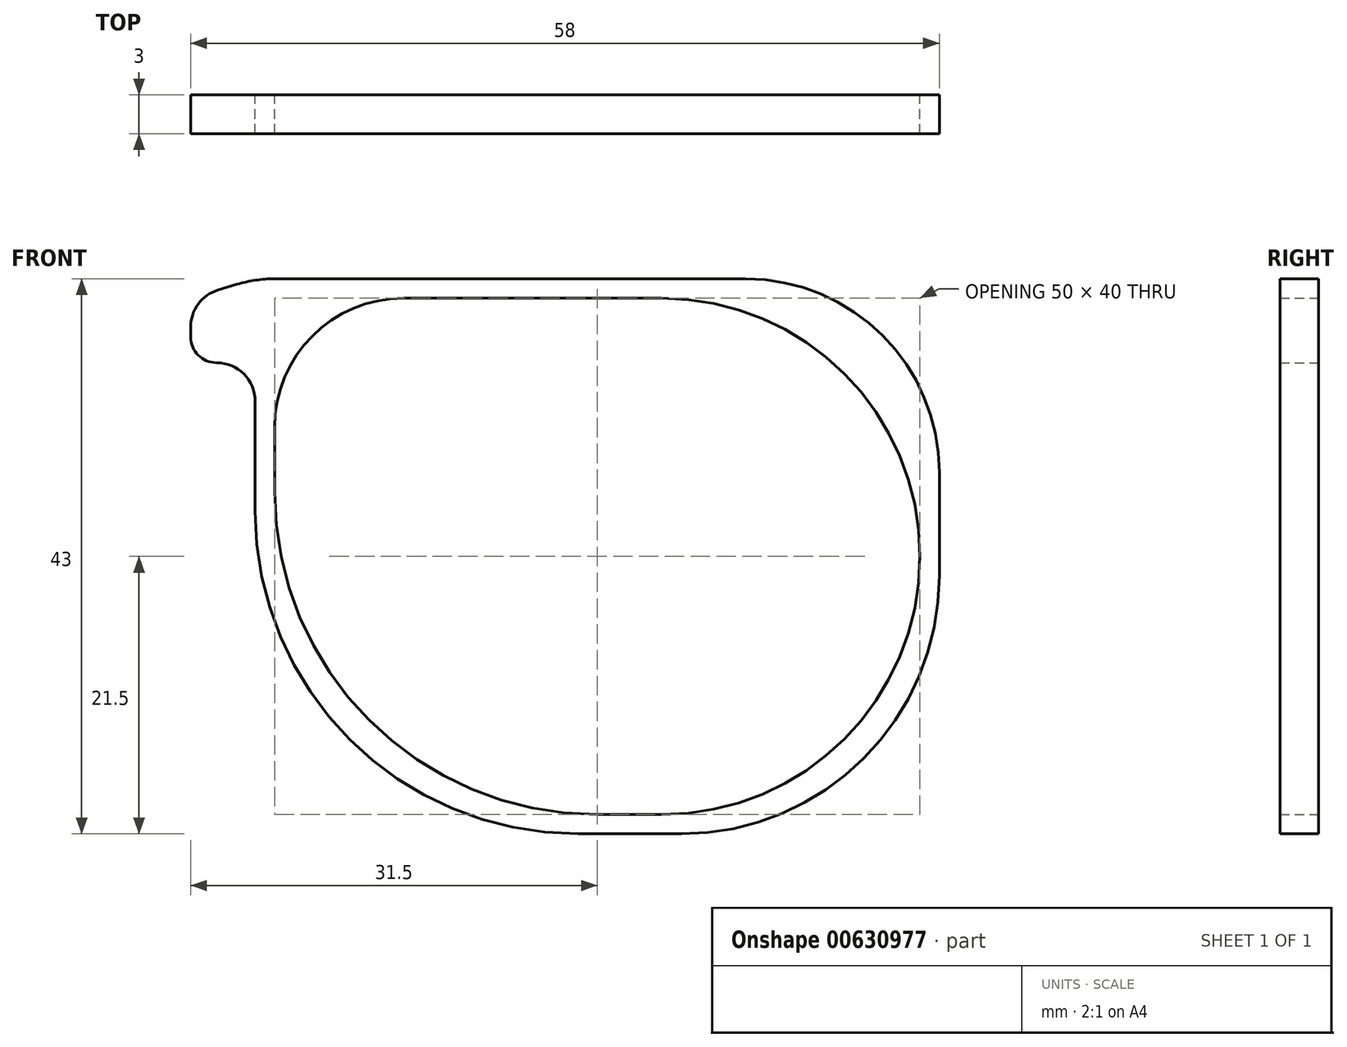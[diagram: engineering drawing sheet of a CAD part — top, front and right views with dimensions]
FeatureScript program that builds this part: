
annotation { "Feature Type Name" : "Feature", "Feature Type Description" : "" }
export const myFeature = defineFeature(function(context is Context, id is Id, definition is map)
    precondition{}
    {
        {
            var Q0;
            Q0=qCreatedBy(makeId("Front.planeOp"),FACE);
            var sketch = newSketch(context, id + "F0", { "sketchPlane" : qUnion([Q0])});
            skLineSegment(sketch, "E0.bottom", {"start": v(5, 20) * mm, "end": v(-15, 20) * mm});
            skLineSegment(sketch, "E0.top", {"start": v(5, -20) * mm, "end": v(0, -20) * mm});
            skLineSegment(sketch, "E0.left", {"start": v(25, 0) * mm, "end": v(25, 0) * mm});
            skLineSegment(sketch, "E0.right", {"start": v(-25, 10) * mm, "end": v(-25, 5) * mm});
            skPoint(sketch, "E0.middle", {"position": v(0, 0) * mm});
            skPoint(sketch, "E1.visualSharp", {"position": v(-25, -20) * mm});
            skArc(sketch, "E1.filletArc", {"start": v(-25, 5) * mm, "mid": v(-17.68, -12.68) * mm, "end": v(0, -20) * mm});
            skPoint(sketch, "E2.visualSharp", {"position": v(25, -20) * mm});
            skArc(sketch, "E2.filletArc", {"start": v(5, -20) * mm, "mid": v(19.14, -14.14) * mm, "end": v(25, 0) * mm});
            skPoint(sketch, "E3.visualSharp", {"position": v(-25, 20) * mm});
            skArc(sketch, "E3.filletArc", {"start": v(-15, 20) * mm, "mid": v(-22.07, 17.07) * mm, "end": v(-25, 10) * mm});
            skPoint(sketch, "E4.visualSharp", {"position": v(25, 20) * mm});
            skArc(sketch, "E4.filletArc", {"start": v(25, 0) * mm, "mid": v(19.14, 14.14) * mm, "end": v(5, 20) * mm});
            skLineSegment(sketch, "E5.bottom", {"start": v(11.5, 21.5) * mm, "end": v(-25.03, 21.5) * mm});
            skLineSegment(sketch, "E5.top", {"start": v(6.5, -21.5) * mm, "end": v(-1.5, -21.5) * mm});
            skLineSegment(sketch, "E5.left", {"start": v(26.5, 6.5) * mm, "end": v(26.5, -1.5) * mm});
            skLineSegment(sketch, "E5.right", {"start": v(-26.5, 12) * mm, "end": v(-26.5, 3.5) * mm});
            skPoint(sketch, "E6.visualSharp", {"position": v(-26.5, -21.5) * mm});
            skArc(sketch, "E6.filletArc", {"start": v(-26.5, 3.5) * mm, "mid": v(-19.18, -14.18) * mm, "end": v(-1.5, -21.5) * mm});
            skPoint(sketch, "E7.visualSharp", {"position": v(26.5, -21.5) * mm});
            skArc(sketch, "E7.filletArc", {"start": v(6.5, -21.5) * mm, "mid": v(20.64, -15.64) * mm, "end": v(26.5, -1.5) * mm});
            skLineSegment(sketch, "E8", {"start": v(-29.5, 15) * mm, "end": v(-29.5, 15) * mm});
            skLineSegment(sketch, "E9", {"start": v(-31.5, 17) * mm, "end": v(-31.5, 17.77) * mm});
            skLineSegment(sketch, "E10", {"start": v(-29.36, 20.64) * mm, "end": v(-27.9, 21.08) * mm});
            skPoint(sketch, "E11.visualSharp", {"position": v(-26.5, 15) * mm});
            skArc(sketch, "E11.filletArc", {"start": v(-26.5, 12) * mm, "mid": v(-27.38, 14.12) * mm, "end": v(-29.5, 15) * mm});
            skPoint(sketch, "E12.visualSharp", {"position": v(-26.5, 21.5) * mm});
            skArc(sketch, "E12.filletArc", {"start": v(-25.03, 21.5) * mm, "mid": v(-26.48, 21.4) * mm, "end": v(-27.9, 21.08) * mm});
            skPoint(sketch, "E13.visualSharp", {"position": v(-31.5, 20) * mm});
            skArc(sketch, "E13.filletArc", {"start": v(-29.36, 20.64) * mm, "mid": v(-30.9, 19.56) * mm, "end": v(-31.5, 17.77) * mm});
            skPoint(sketch, "E14.visualSharp", {"position": v(-31.5, 15) * mm});
            skArc(sketch, "E14.filletArc", {"start": v(-31.5, 17) * mm, "mid": v(-30.91, 15.59) * mm, "end": v(-29.5, 15) * mm});
            skPoint(sketch, "E15.visualSharp", {"position": v(26.5, 21.5) * mm});
            skArc(sketch, "E15.filletArc", {"start": v(26.5, 6.5) * mm, "mid": v(22.1, 17.1) * mm, "end": v(11.5, 21.5) * mm});
            skSolve(sketch);
        }
        {
            var Q0;
            Q0 = qSketchRegion(id + "F0", true);
            extrude(context, id + "F1", {"entities" : qUnion([Q0]), "depth" : 3 * mm, "offsetDistance" : 25 * mm});
        }
    });
